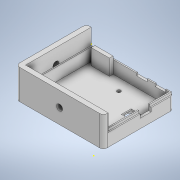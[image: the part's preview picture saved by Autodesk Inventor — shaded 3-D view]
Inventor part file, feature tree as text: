
AUTODESK INVENTOR PART (.ipt)
format: ipt  version: 2022 (Build 260153000, 153)  size: 305,664 bytes
history: native  units: in
note: dims shown in document units (in); Inventor stores cm internally (conversion verified against a paired STEP export)
features: extrude x12, sketch x10, fillet x4
ambient origin geometry x8: Origin, YZ Plane, XZ Plane, XY Plane, X Axis, Y Axis, Z Axis, Center Point
bodies: Solid1 (feature_tree)
feature tree (26):
  sketch  "Sketch1"  dims[d0=2.6772in d2=0.4921in d3=0.0in]
  extrude  "Extrusion1"  Depth=0.4921in TaperAngle=0.0deg
  sketch  "Sketch3"  dims[d5=0.0787in d6=0.0787in]
  extrude  "Extrusion2"  Depth=0.0787in
  extrude  "Extrusion3"  Depth=0.0787in
  extrude  "Extrusion4"  Depth=0.0787in TaperAngle=0.0deg
  extrude  "Extrusion5"  Depth=0.0787in TaperAngle=0.0deg
  extrude  "Extrusion6"  Depth=0.1181in
  extrude  "Extrusion7"  Depth=0.5118in TaperAngle=0.0deg
  extrude  "Extrusion9"  Depth=0.0787in
  fillet  "Fillet7"  Radius=0.0394in
  fillet  "Fillet9"  Radius=0.1181in
  extrude  "Extrusion11"  Depth=0.9646in TaperAngle=0.0deg
  extrude  "Extrusion12"  Depth=0.0197in
  extrude  "Extrusion13"  Depth=0.315in
  extrude  "Extrusion14"  Depth=0.1181in
  fillet  "Fillet12"  Radius=0.3543in
  fillet  "Fillet13"  Radius=1.0933in
  sketch  "Sketch4"  dims[d7=0.0787in d11=0.0787in]
  sketch  "Sketch7"  dims[d13=0.4134in d14=0.0in d44=0.0787in d45=0.0in]
  sketch  "Sketch10"  dims[d46=2.6772in d48=0.0787in d49=0.0in]
  sketch  "Sketch11"  dims[d57=0.5906in d58=0.1181in]
  sketch  "Sketch17"  dims[d61=0.5906in d64=0.5118in d65=0.0in]
  sketch  "Sketch18"  dims[d72=0.3543in d73=0.0in d75=0.0787in d76=0.0394in d79=0.1181in]
  sketch  "Sketch19"  dims[d81=0.1575in d82=0.9646in d83=0.0in]
  sketch  "Sketch20"  dims[d85=0.9161in d86=0.8465in d88=0.315in d89=0.1181in d108=0.3543in d109=0.1969in d111=1.0933in d114=0.3937in d115=0.0in d119=0.4528in d120=0.3937in d121=0.1181in d123=0.1181in d132=1.9685in d133=2.5197in d138=2.126in d139=0.0394in d140=0.0394in d141=0.0394in d144=0.0in d151=0.3346in d152=0.3346in d153=0.1969in d157=0.0in d158=0.5315in d160=1.126in d161=0.3937in d162=0.0in d169=0.1575in d170=0.315in d171=0.315in d172=0.0394in d173=0.0in d174=0.0in d177=1.4173in d178=0.1969in d179=0.1575in d180=0.0in d181=0.1969in d182=0.1575in d183=0.0in d184=0.1181in d185=0.1181in d40=0.0197in d41=0.0344in d42=0.0197in d43=0.0344in d66=0.0197in d67=0.0344in d84=0.0197in]
